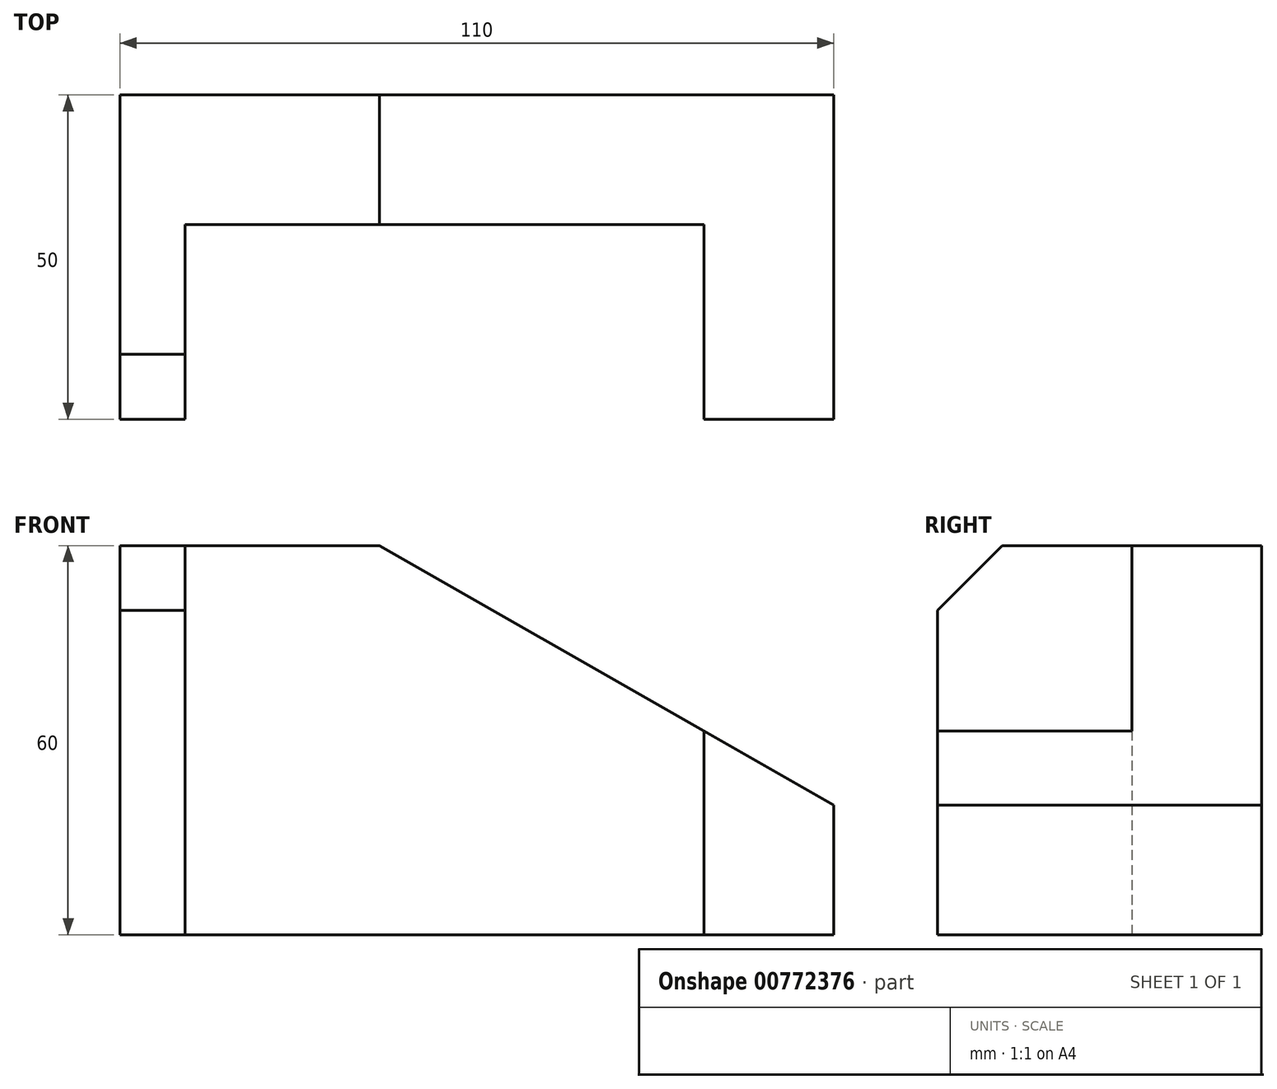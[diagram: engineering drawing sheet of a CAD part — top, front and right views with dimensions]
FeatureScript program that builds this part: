
annotation { "Feature Type Name" : "Feature", "Feature Type Description" : "" }
export const myFeature = defineFeature(function(context is Context, id is Id, definition is map)
    precondition{}
    {
        {
            var Q0;
            Q0=qCreatedBy(makeId("Top.planeOp"),FACE);
            var sketch = newSketch(context, id + "F0", { "sketchPlane" : qUnion([Q0])});
            skLineSegment(sketch, "E0", {"start": v(0, 0) * mm, "end": v(0, 50) * mm});
            skLineSegment(sketch, "E1", {"start": v(0, 50) * mm, "end": v(110, 50) * mm});
            skLineSegment(sketch, "E2", {"start": v(110, 50) * mm, "end": v(110, 0) * mm});
            skLineSegment(sketch, "E3", {"start": v(110, 0) * mm, "end": v(90, 0) * mm});
            skLineSegment(sketch, "E4", {"start": v(90, 0) * mm, "end": v(90, 30) * mm});
            skLineSegment(sketch, "E5", {"start": v(90, 30) * mm, "end": v(10, 30) * mm});
            skLineSegment(sketch, "E6", {"start": v(10, 30) * mm, "end": v(10, 0) * mm});
            skLineSegment(sketch, "E7", {"start": v(10, 0) * mm, "end": v(0, 0) * mm});
            skSolve(sketch);
        }
        {
            var Q0;
            Q0=makeQuery(id+"F0.imprint","IMPRINT",FACE,{"disambiguationData":[TD([[makeQuery(id+"F0.imprint","IMPRINT",EDGE,{"derivedFrom":sQuery(id+"F0.wireOp",EDGE,"E0")}),-1.0]])]});
            extrude(context, id + "F1", {"entities" : qUnion([Q0]), "depth" : 60 * mm, "offsetDistance" : 25 * mm});
        }
        {
            var Q0;
            Q0=makeQuery(id+"F1.opExtrude","CAP_EDGE",EDGE,{"disambiguationData":[OSD([sQuery(id+"F0.wireOp",EDGE,"E7")])],"isStart":false});
            chamfer(context, id + "F2", {"entities" : qUnion([Q0]), "width" : 10 * mm, "tangentPropagation" : true});
        }
        {
            var Q0;
            Q0=makeQuery(id+"F1.opExtrude","CAP_EDGE",EDGE,{"disambiguationData":[OSD([sQuery(id+"F0.wireOp",EDGE,"E2")])],"isStart":false});
            chamfer(context, id + "F3", {"entities" : qUnion([Q0]), "chamferType" : ChamferType.TWO_OFFSETS, "width1" : 40 * mm, "oppositeDirection" : false, "width2" : 70 * mm, "tangentPropagation" : true});
        }
    });
